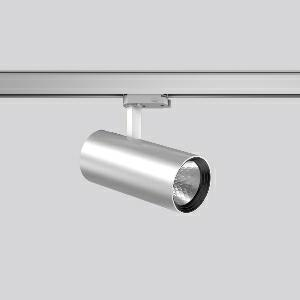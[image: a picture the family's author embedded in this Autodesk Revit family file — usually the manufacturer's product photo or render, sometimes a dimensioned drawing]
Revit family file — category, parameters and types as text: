
# Revit family: deecos_s_mini_742197_004_3_76_1293
name_source: partatom
category: Lighting Fixtures
units: mm (PartAtom-declared; Revit-internal decimal feet)

## family parameters
Cut with Voids When Loaded = No
Host = Face
Light Source = No
Part Type = Normal
Room Calculation Point = No
Round Connector Dimension = Use Diameter
Shared = No

## types (1)
- DEECOS S mini (1 x LED Modul 935, 2650 lm, 3500)
    Apparent Load = 20 VA
    Approval mark = CE
    CIE Flux Codes = 95 99 100 100 100
    Color Rendering = 92
    Color Temperature = 3500
    Default Elevation = 1800 mm
    Description = Series: DEECOS S mini
LED surface-mounted projector in modern design with no visible cooling ribs. Housing: die-cast aluminium, powder-coated. Rotation range: 356°. Swivel range: 90°. Black plastic ring and recessed LED to prevent glare from the side. Optical assembly with reflector made of MIRO-Silver with 98% total light reflection for outstanding efficiency - can be changed without tools. Best colour rendering index Ra>90. With adapter for RZB 3-circuit DALI tracks. Suitable for Track on ceiling, Wall track. High quality converter without flickering and stroboscopic effect. The following accessories can be mounted without use of tools: interchangeable lenses, decorative glasses, honeycomb louvre, clear and frosted diffusers, white interchangeable plastic ring. 
Colour: silver
Diameter: 87 mm
Height: 214 mm
Lamp: LED
Socket: without socket
Colour temperature: 3500K
Colour rendering index (CRI): 92
System power: 20 W
Rated luminous flux: 2650 lm
Luminous efficiency: 133 lm/W
Control gear: Converter, dimmable, DALI
Protection class: I
Type of protection: IP 20
    Height = 214 mm
    Lamp = 1 x LED Modul 935
    Lamp Light Flux = 2650 lm
    Lamp count = 1
    Length = 87 mm
    Lifetime = 50000 h
    Luminous efficacy = 133 lm/W
    Manufacturer = RZB
    ModVariant = No
    Model = 742197.004.3.76
    Mounting Place = Ceiling
    Mounting Type = Rail mounted
    Number of Poles = 1
    OnlyDefault = Yes
    Power Factor = 1
    Product Name = DEECOS S mini
    Product group = Track mounted projectors
    ProductGroupID = 301
    Protection Class = Protection class I
    Protection Degree = IP 20
    RLX_Detail_Level = 1
    RLX_Emergency_Light_Flux = 0 lm
    RLX_Emergency_Type = 0
    RLX_Emergency_Type_DB = No
    RlxData = <blob elided: 37149 chars, md5=a66f5010>
    Socket = socket
    Standby Power = 0 W
    System Light Flux = 2650 lm
    System Power = 20 W
    Type Comments = Product without accessories
    Type Image = 741926.004.jpg
    URL = http://relux.com
    VarID = ---
    Voltage = 230 V
    Voltage Range = 220-240 V
    Weight = 0.00 kg
    Width = 0 mm  [stored 0 ft]

note: [stored X ft] marks values corroborated as IEEE doubles in the binary element streams (Revit-internal decimal feet)

## geometry (parser evidence)
native form markers: Blend x4, Sweep x13
no freeform markers — native parametric forms only
